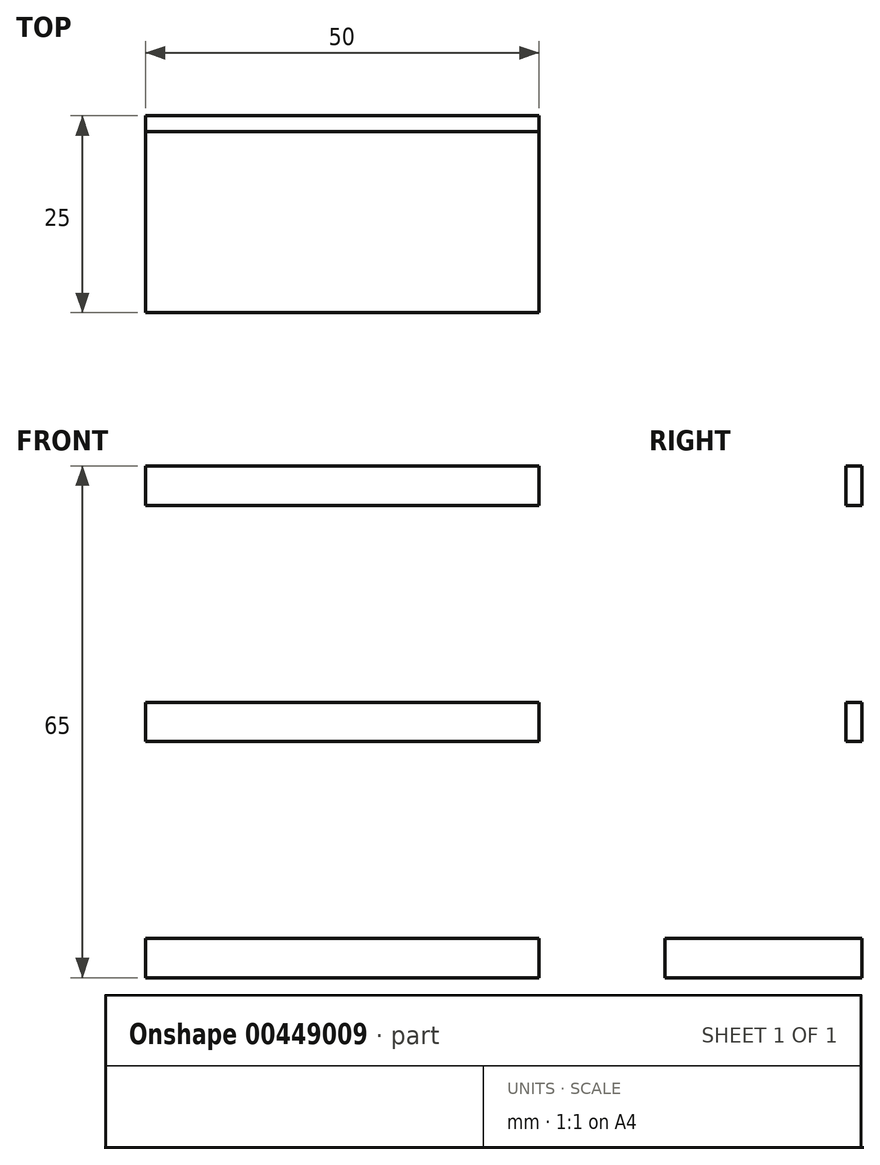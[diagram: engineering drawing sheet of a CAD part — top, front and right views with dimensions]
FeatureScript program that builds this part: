
annotation { "Feature Type Name" : "Feature", "Feature Type Description" : "" }
export const myFeature = defineFeature(function(context is Context, id is Id, definition is map)
    precondition{}
    {
        {
            var Q0;
            Q0=qCreatedBy(makeId("Front.planeOp"),FACE);
            var sketch = newSketch(context, id + "F0", { "sketchPlane" : qUnion([Q0])});
            skLineSegment(sketch, "E0.bottom", {"start": v(0, 0) * mm, "end": v(50, 0) * mm});
            skLineSegment(sketch, "E0.top", {"start": v(0, 5) * mm, "end": v(50, 5) * mm});
            skLineSegment(sketch, "E0.left", {"start": v(0, 0) * mm, "end": v(0, 5) * mm});
            skLineSegment(sketch, "E0.right", {"start": v(50, 0) * mm, "end": v(50, 5) * mm});
            skLineSegment(sketch, "E1.bottom", {"start": v(0, 5) * mm, "end": v(5, 5) * mm});
            skLineSegment(sketch, "E1.top", {"start": v(0, 30) * mm, "end": v(5, 30) * mm});
            skLineSegment(sketch, "E1.left", {"start": v(0, 5) * mm, "end": v(0, 30) * mm});
            skLineSegment(sketch, "E1.right", {"start": v(5, 5) * mm, "end": v(5, 30) * mm});
            skLineSegment(sketch, "E2.bottom", {"start": v(0, 30) * mm, "end": v(50, 30) * mm});
            skLineSegment(sketch, "E2.top", {"start": v(0, 35) * mm, "end": v(50, 35) * mm});
            skLineSegment(sketch, "E2.left", {"start": v(0, 30) * mm, "end": v(0, 35) * mm});
            skLineSegment(sketch, "E2.right", {"start": v(50, 30) * mm, "end": v(50, 35) * mm});
            skLineSegment(sketch, "E3.bottom", {"start": v(0, 35) * mm, "end": v(5, 35) * mm});
            skLineSegment(sketch, "E3.top", {"start": v(0, 60) * mm, "end": v(5, 60) * mm});
            skLineSegment(sketch, "E3.left", {"start": v(0, 35) * mm, "end": v(0, 60) * mm});
            skLineSegment(sketch, "E3.right", {"start": v(5, 35) * mm, "end": v(5, 60) * mm});
            skLineSegment(sketch, "E4.bottom", {"start": v(0, 60) * mm, "end": v(50, 60) * mm});
            skLineSegment(sketch, "E4.top", {"start": v(0, 65) * mm, "end": v(50, 65) * mm});
            skLineSegment(sketch, "E4.left", {"start": v(0, 60) * mm, "end": v(0, 65) * mm});
            skLineSegment(sketch, "E4.right", {"start": v(50, 60) * mm, "end": v(50, 65) * mm});
            skSolve(sketch);
        }
        {
            var Q0;
            Q0=makeQuery(id+"F0.imprint","IMPRINT",FACE,{"disambiguationData":[TD([[makeQuery(id+"F0.imprint","IMPRINT",EDGE,{"derivedFrom":sQuery(id+"F0.wireOp",EDGE,"E0.bottom")}),1.0]])]});
            var Q1;
            Q1=makeQuery(id+"F0.imprint","IMPRINT",FACE,{"disambiguationData":[TD([[makeQuery(id+"F0.imprint","IMPRINT",EDGE,{"derivedFrom":sQuery(id+"F0.wireOp",EDGE,"E1.bottom")}),1.0]])]});
            extrude(context, id + "F1", {"entities" : qUnion([Q0, Q1]), "depth" : 25 * mm});
        }
        {
            var Q0;
            Q0=makeQuery(id+"F0.imprint","IMPRINT",FACE,{"disambiguationData":[TD([[makeQuery(id+"F0.imprint","IMPRINT",EDGE,{"derivedFrom":sQuery(id+"F0.wireOp",EDGE,"E4.top")}),-1.0]])]});
            var Q1;
            Q1=makeQuery(id+"F0.imprint","IMPRINT",FACE,{"disambiguationData":[TD([[makeQuery(id+"F0.imprint","IMPRINT",EDGE,{"derivedFrom":sQuery(id+"F0.wireOp",EDGE,"E3.bottom")}),1.0]])]});
            var Q2;
            Q2=makeQuery(id+"F0.imprint","IMPRINT",FACE,{"disambiguationData":[TD([[makeQuery(id+"F0.imprint","IMPRINT",EDGE,{"derivedFrom":sQuery(id+"F0.wireOp",EDGE,"E2.top")}),-1.0]])]});
            extrude(context, id + "F2", {"entities" : qUnion([Q0, Q1, Q2]), "operationType" : NewBodyOperationType.ADD, "depth" : 2 * mm});
        }
    });
